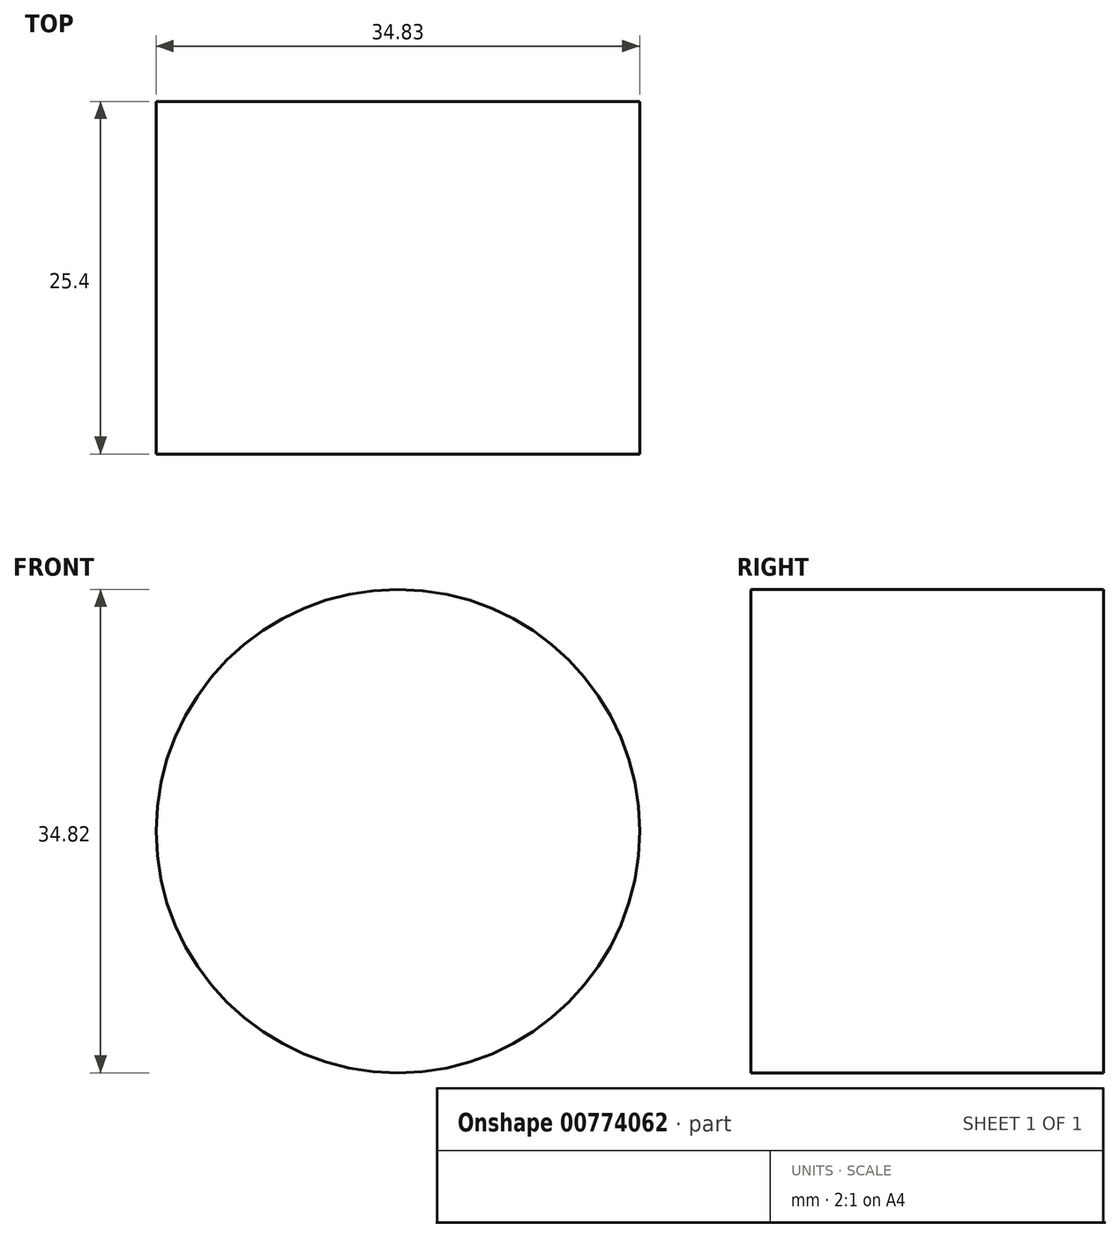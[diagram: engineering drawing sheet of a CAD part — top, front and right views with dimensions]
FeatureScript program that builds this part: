
annotation { "Feature Type Name" : "Feature", "Feature Type Description" : "" }
export const myFeature = defineFeature(function(context is Context, id is Id, definition is map)
    precondition{}
    {
        {
            var Q0;
            Q0=qCreatedBy(makeId("Front.planeOp"),FACE);
            var sketch = newSketch(context, id + "F0", { "sketchPlane" : qUnion([Q0])});
            skCircle(sketch, "E0", {"center": v(0, 0) * mm, "radius": 31.75 * mm});
            skCircle(sketch, "E1", {"center": v(106.66, 0) * mm, "radius": 17.41 * mm});
            skSolve(sketch);
        }
        {
            var Q0;
            Q0=sQuery(id+"F0.wireOp",EDGE,"E1");
            extrude(context, id + "F1", {"bodyType" : ToolBodyType.SURFACE, "surfaceEntities" : qUnion([Q0]), "depth" : 25.4 * mm, "offsetDistance" : 25.4 * mm});
        }
    });
